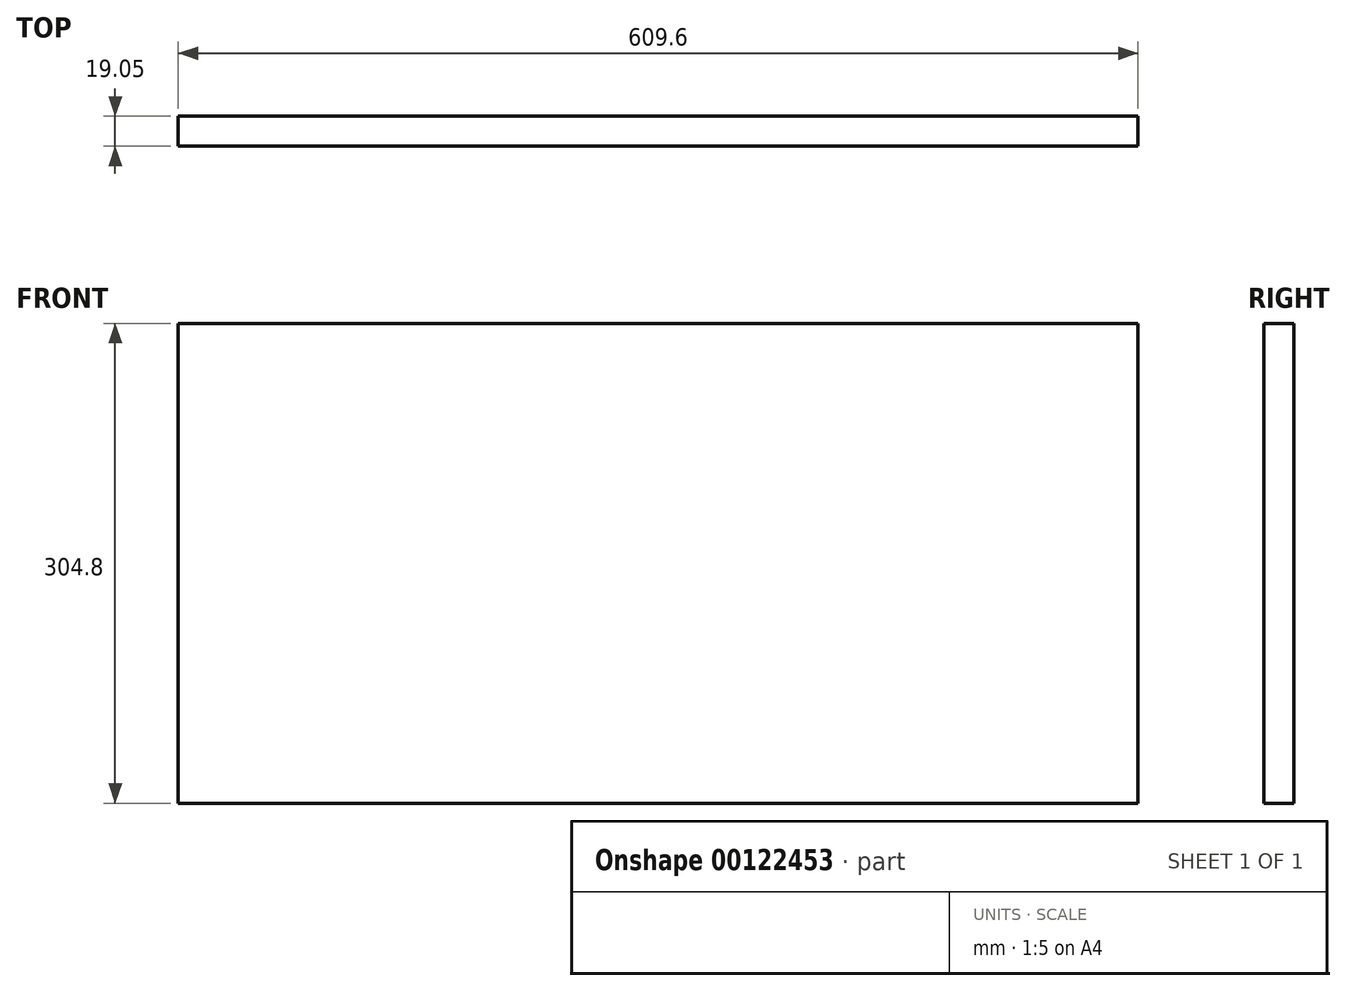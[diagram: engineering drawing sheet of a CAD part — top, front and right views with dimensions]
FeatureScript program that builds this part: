
annotation { "Feature Type Name" : "Feature", "Feature Type Description" : "" }
export const myFeature = defineFeature(function(context is Context, id is Id, definition is map)
    precondition{}
    {
        {
            var Q0;
            Q0=qCreatedBy(makeId("Front.planeOp"),FACE);
            var sketch = newSketch(context, id + "F0", { "sketchPlane" : qUnion([Q0])});
            skLineSegment(sketch, "E0.bottom", {"start": v(0, 0) * mm, "end": v(609.6, 0) * mm});
            skLineSegment(sketch, "E0.top", {"start": v(0, 304.8) * mm, "end": v(609.6, 304.8) * mm});
            skLineSegment(sketch, "E0.left", {"start": v(0, 0) * mm, "end": v(0, 304.8) * mm});
            skLineSegment(sketch, "E0.right", {"start": v(609.6, 0) * mm, "end": v(609.6, 304.8) * mm});
            skSolve(sketch);
        }
        {
            var Q0;
            Q0 = qSketchRegion(id + "F0", true);
            extrude(context, id + "F1", {"entities" : qUnion([Q0]), "depth" : 19.05 * mm});
        }
    });
